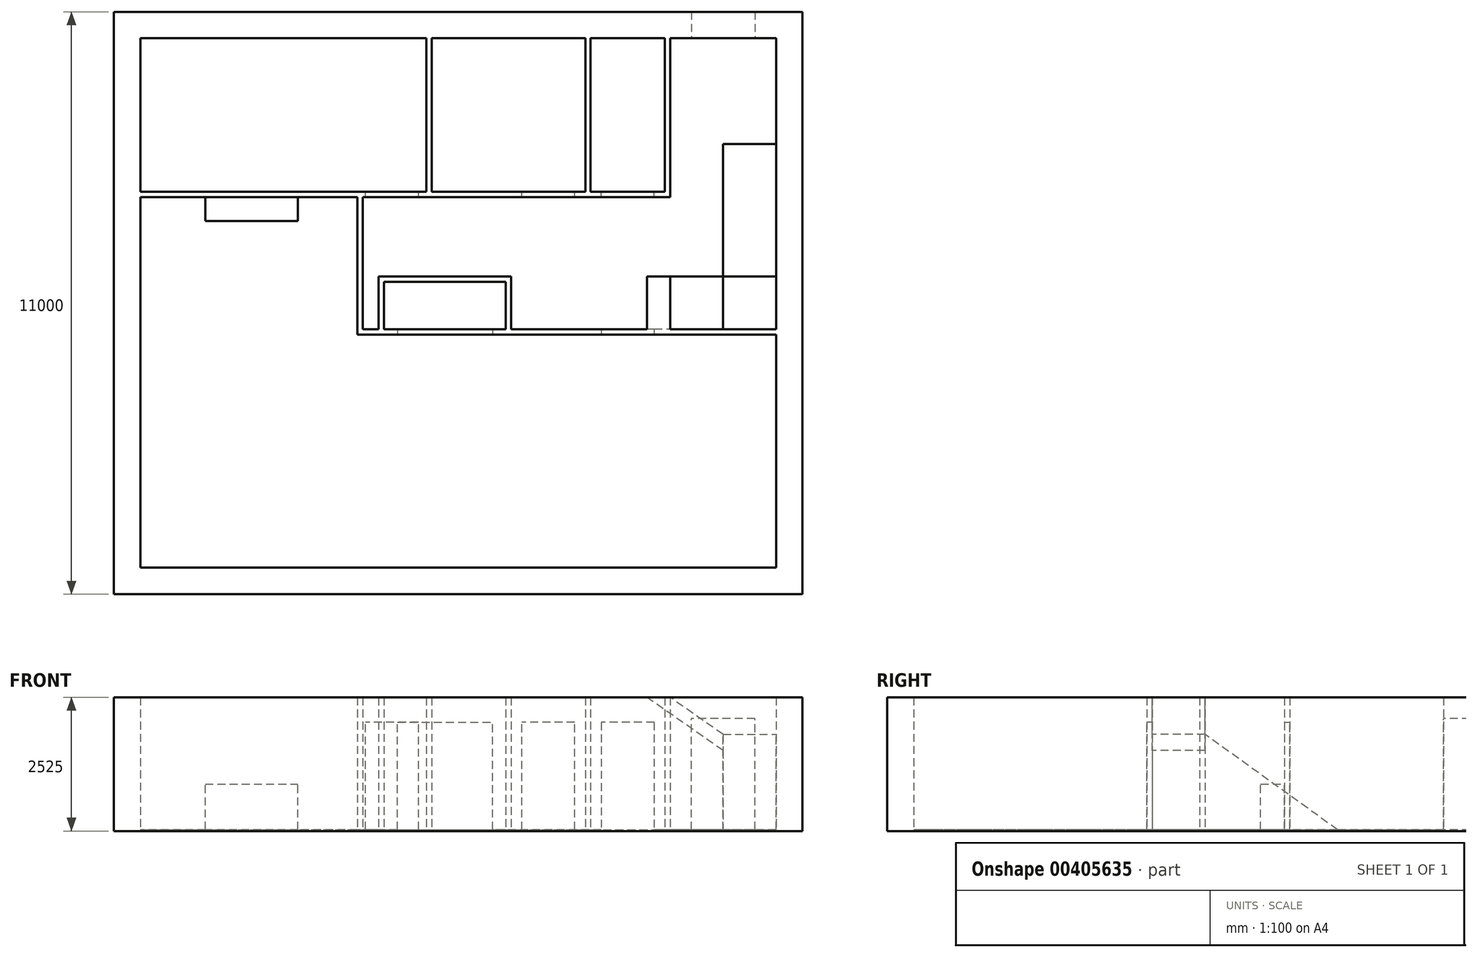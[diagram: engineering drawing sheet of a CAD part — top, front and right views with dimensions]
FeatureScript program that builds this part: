
annotation { "Feature Type Name" : "Feature", "Feature Type Description" : "" }
export const myFeature = defineFeature(function(context is Context, id is Id, definition is map)
    precondition{}
    {
        {
            var Q0;
            Q0=qCreatedBy(makeId("Top.planeOp"),FACE);
            var sketch = newSketch(context, id + "F0", { "sketchPlane" : qUnion([Q0])});
            skLineSegment(sketch, "E0.bottom", {"start": v(0, 0) * mm, "end": v(-13000, 0) * mm});
            skLineSegment(sketch, "E0.top", {"start": v(0, -11000) * mm, "end": v(-13000, -11000) * mm});
            skLineSegment(sketch, "E0.left", {"start": v(0, 0) * mm, "end": v(0, -11000) * mm});
            skLineSegment(sketch, "E0.right", {"start": v(-13000, 0) * mm, "end": v(-13000, -11000) * mm});
            skLineSegment(sketch, "E1.bottom", {"start": v(-12500, -500) * mm, "end": v(-7100, -500) * mm});
            skLineSegment(sketch, "E1.top", {"start": v(-12500, -10500) * mm, "end": v(-500, -10500) * mm});
            skLineSegment(sketch, "E1.left", {"start": v(-12500, -500) * mm, "end": v(-12500, -3400) * mm});
            skLineSegment(sketch, "E1.right", {"start": v(-500, -500) * mm, "end": v(-500, -6000) * mm});
            skLineSegment(sketch, "E2", {"start": v(-500, -6000) * mm, "end": v(-5500, -6000) * mm});
            skLineSegment(sketch, "E3", {"start": v(-8300, -6000) * mm, "end": v(-8300, -3500) * mm});
            skLineSegment(sketch, "E4", {"start": v(-8300, -3500) * mm, "end": v(-12500, -3500) * mm});
            skLineSegment(sketch, "E5", {"start": v(-8300, -3500) * mm, "end": v(-2500, -3500) * mm});
            skLineSegment(sketch, "E6", {"start": v(-2500, -3500) * mm, "end": v(-2500, -500) * mm});
            skLineSegment(sketch, "E7", {"start": v(-7000, -3400) * mm, "end": v(-7000, -500) * mm});
            skLineSegment(sketch, "E8", {"start": v(-8000, -5000) * mm, "end": v(-5500, -5000) * mm});
            skLineSegment(sketch, "E9", {"start": v(-5500, -5000) * mm, "end": v(-5500, -6000) * mm});
            skLineSegment(sketch, "E10", {"start": v(-8000, -5000) * mm, "end": v(-8000, -6000) * mm});
            skLineSegment(sketch, "E11", {"start": v(-500, -6100) * mm, "end": v(-8400, -6100) * mm});
            skLineSegment(sketch, "E12", {"start": v(-8400, -6100) * mm, "end": v(-8400, -3500) * mm});
            skLineSegment(sketch, "E13", {"start": v(-7900, -6000) * mm, "end": v(-7900, -5100) * mm});
            skLineSegment(sketch, "E14", {"start": v(-7900, -5100) * mm, "end": v(-5600, -5100) * mm});
            skLineSegment(sketch, "E15", {"start": v(-5600, -5100) * mm, "end": v(-5600, -6000) * mm});
            skLineSegment(sketch, "E16.trimOffspring", {"start": v(-8000, -6000) * mm, "end": v(-8300, -6000) * mm});
            skLineSegment(sketch, "E17.trimOffspring", {"start": v(-5600, -6000) * mm, "end": v(-7900, -6000) * mm});
            skLineSegment(sketch, "E18.trimOffspring", {"start": v(-500, -6100) * mm, "end": v(-500, -10500) * mm});
            skLineSegment(sketch, "E19", {"start": v(-12500, -3400) * mm, "end": v(-7100, -3400) * mm});
            skLineSegment(sketch, "E20", {"start": v(-2600, -3400) * mm, "end": v(-2600, -500) * mm});
            skLineSegment(sketch, "E21", {"start": v(-4100, -3400) * mm, "end": v(-4100, -500) * mm});
            skLineSegment(sketch, "E22", {"start": v(-7100, -3400) * mm, "end": v(-7100, -500) * mm});
            skLineSegment(sketch, "E23.trimOffspring", {"start": v(-7000, -500) * mm, "end": v(-4100, -500) * mm});
            skLineSegment(sketch, "E24.trimOffspring", {"start": v(-7000, -3400) * mm, "end": v(-4100, -3400) * mm});
            skLineSegment(sketch, "E25.trimOffspring", {"start": v(-4000, -3400) * mm, "end": v(-2600, -3400) * mm});
            skLineSegment(sketch, "E26", {"start": v(-4000, -3400) * mm, "end": v(-4000, -500) * mm});
            skLineSegment(sketch, "E27.trimOffspring", {"start": v(-4000, -500) * mm, "end": v(-2600, -500) * mm});
            skLineSegment(sketch, "E28.trimOffspring", {"start": v(-2500, -500) * mm, "end": v(-500, -500) * mm});
            skLineSegment(sketch, "E29.trimOffspring", {"start": v(-12500, -3500) * mm, "end": v(-12500, -10500) * mm});
            skSolve(sketch);
        }
        {
            var Q0;
            Q0 = qSketchRegion(id + "F0", true);
            extrude(context, id + "F1", {"entities" : qUnion([Q0]), "depth" : 2500 * mm});
        }
        {
            var Q0;
            Q0=makeQuery(id+"F1.opExtrude","SWEPT_FACE",FACE,{"disambiguationData":[OSD([sQuery(id+"F0.wireOp",EDGE,"E28.trimOffspring")])]});
            var sketch = newSketch(context, id + "F2", { "sketchPlane" : qUnion([Q0])});
            skLineSegment(sketch, "E30.bottom", {"start": v(-900, 0) * mm, "end": v(-2100, 0) * mm});
            skLineSegment(sketch, "E30.top", {"start": v(-900, 2100) * mm, "end": v(-2100, 2100) * mm});
            skLineSegment(sketch, "E30.left", {"start": v(-900, 0) * mm, "end": v(-900, 2100) * mm});
            skLineSegment(sketch, "E30.right", {"start": v(-2100, 0) * mm, "end": v(-2100, 2100) * mm});
            skSolve(sketch);
        }
        {
            var Q0;
            Q0 = qSketchRegion(id + "F2", true);
            extrude(context, id + "F3", {"entities" : qUnion([Q0]), "operationType" : NewBodyOperationType.REMOVE, "endBound" : BoundingType.UP_TO_NEXT, "oppositeDirection" : true, "depth" : 25 * mm});
        }
        {
            var Q0;
            Q0=makeQuery(id+"F1.opExtrude","SWEPT_FACE",FACE,{"disambiguationData":[OSD([sQuery(id+"F0.wireOp",EDGE,"E25.trimOffspring")])]});
            var sketch = newSketch(context, id + "F4", { "sketchPlane" : qUnion([Q0])});
            skLineSegment(sketch, "E31.bottom", {"start": v(2800, 0) * mm, "end": v(3800, 0) * mm});
            skLineSegment(sketch, "E31.top", {"start": v(2800, 2030) * mm, "end": v(3800, 2030) * mm});
            skLineSegment(sketch, "E31.left", {"start": v(2800, 0) * mm, "end": v(2800, 2030) * mm});
            skLineSegment(sketch, "E31.right", {"start": v(3800, 0) * mm, "end": v(3800, 2030) * mm});
            skLineSegment(sketch, "E32.bottom", {"start": v(4300, 0) * mm, "end": v(5300, 0) * mm});
            skLineSegment(sketch, "E32.top", {"start": v(4300, 2030) * mm, "end": v(5300, 2030) * mm});
            skLineSegment(sketch, "E32.left", {"start": v(4300, 0) * mm, "end": v(4300, 2030) * mm});
            skLineSegment(sketch, "E32.right", {"start": v(5300, 0) * mm, "end": v(5300, 2030) * mm});
            skLineSegment(sketch, "E33.bottom", {"start": v(7250, 0) * mm, "end": v(8250, 0) * mm});
            skLineSegment(sketch, "E33.top", {"start": v(7250, 2030) * mm, "end": v(8250, 2030) * mm});
            skLineSegment(sketch, "E33.left", {"start": v(7250, 0) * mm, "end": v(7250, 2030) * mm});
            skLineSegment(sketch, "E33.right", {"start": v(8250, 0) * mm, "end": v(8250, 2030) * mm});
            skSolve(sketch);
        }
        {
            var Q0;
            Q0 = qSketchRegion(id + "F4", true);
            extrude(context, id + "F5", {"entities" : qUnion([Q0]), "operationType" : NewBodyOperationType.REMOVE, "endBound" : BoundingType.UP_TO_NEXT, "oppositeDirection" : true, "depth" : 25 * mm});
        }
        {
            var Q0;
            Q0=makeQuery(id+"F1.opExtrude","SWEPT_FACE",FACE,{"disambiguationData":[OSD([sQuery(id+"F0.wireOp",EDGE,"E11")])]});
            var sketch = newSketch(context, id + "F6", { "sketchPlane" : qUnion([Q0])});
            skLineSegment(sketch, "E34.bottom", {"start": v(-7650, 0) * mm, "end": v(-5850, 0) * mm});
            skLineSegment(sketch, "E34.top", {"start": v(-7650, 2030) * mm, "end": v(-5850, 2030) * mm});
            skLineSegment(sketch, "E34.left", {"start": v(-7650, 0) * mm, "end": v(-7650, 2030) * mm});
            skLineSegment(sketch, "E34.right", {"start": v(-5850, 0) * mm, "end": v(-5850, 2030) * mm});
            skLineSegment(sketch, "E35.bottom", {"start": v(-3800, 0) * mm, "end": v(-2800, 0) * mm});
            skLineSegment(sketch, "E35.top", {"start": v(-3800, 2030) * mm, "end": v(-2800, 2030) * mm});
            skLineSegment(sketch, "E35.left", {"start": v(-3800, 0) * mm, "end": v(-3800, 2030) * mm});
            skLineSegment(sketch, "E35.right", {"start": v(-2800, 0) * mm, "end": v(-2800, 2030) * mm});
            skSolve(sketch);
        }
        {
            var Q0;
            Q0 = qSketchRegion(id + "F6", true);
            extrude(context, id + "F7", {"entities" : qUnion([Q0]), "operationType" : NewBodyOperationType.REMOVE, "endBound" : BoundingType.UP_TO_NEXT, "oppositeDirection" : true, "depth" : 25 * mm});
        }
        {
            var Q0;
            Q0=makeQuery(id+"F1.opExtrude","SWEPT_FACE",FACE,{"disambiguationData":[OSD([sQuery(id+"F0.wireOp",EDGE,"E4")])]});
            var sketch = newSketch(context, id + "F8", { "sketchPlane" : qUnion([Q0])});
            skLineSegment(sketch, "E36.bottom", {"start": v(-11275, 0) * mm, "end": v(-9525, 0) * mm});
            skLineSegment(sketch, "E36.top", {"start": v(-11275, 860) * mm, "end": v(-9525, 860) * mm});
            skLineSegment(sketch, "E36.left", {"start": v(-11275, 0) * mm, "end": v(-11275, 860) * mm});
            skLineSegment(sketch, "E36.right", {"start": v(-9525, 0) * mm, "end": v(-9525, 860) * mm});
            skSolve(sketch);
        }
        {
            var Q0;
            Q0 = qSketchRegion(id + "F8", true);
            extrude(context, id + "F9", {"entities" : qUnion([Q0]), "operationType" : NewBodyOperationType.ADD, "depth" : 450 * mm});
        }
        {
            var Q0;
            Q0=makeQuery(id+"F9.boolean.opBoolean","MERGE",FACE,{"derivedFrom":[makeQuery(id+"F1.opExtrude","CAP_FACE",FACE,{"disambiguationData":[OSD([sQuery(id+"F0.wireOp",EDGE,"E0.bottom"),sQuery(id+"F0.wireOp",EDGE,"E0.top"),sQuery(id+"F0.wireOp",EDGE,"E0.left"),sQuery(id+"F0.wireOp",EDGE,"E0.right"),sQuery(id+"F0.wireOp",EDGE,"E1.bottom"),sQuery(id+"F0.wireOp",EDGE,"E1.top"),sQuery(id+"F0.wireOp",EDGE,"E1.left"),sQuery(id+"F0.wireOp",EDGE,"E1.right"),sQuery(id+"F0.wireOp",EDGE,"E2"),sQuery(id+"F0.wireOp",EDGE,"E3"),sQuery(id+"F0.wireOp",EDGE,"E4"),sQuery(id+"F0.wireOp",EDGE,"E5"),sQuery(id+"F0.wireOp",EDGE,"E6"),sQuery(id+"F0.wireOp",EDGE,"E7"),sQuery(id+"F0.wireOp",EDGE,"E8"),sQuery(id+"F0.wireOp",EDGE,"E9"),sQuery(id+"F0.wireOp",EDGE,"E10"),sQuery(id+"F0.wireOp",EDGE,"E11"),sQuery(id+"F0.wireOp",EDGE,"E12"),sQuery(id+"F0.wireOp",EDGE,"E13"),sQuery(id+"F0.wireOp",EDGE,"E14"),sQuery(id+"F0.wireOp",EDGE,"E15"),sQuery(id+"F0.wireOp",EDGE,"E16.trimOffspring"),sQuery(id+"F0.wireOp",EDGE,"E17.trimOffspring"),sQuery(id+"F0.wireOp",EDGE,"E18.trimOffspring"),sQuery(id+"F0.wireOp",EDGE,"E19"),sQuery(id+"F0.wireOp",EDGE,"E20"),sQuery(id+"F0.wireOp",EDGE,"E21"),sQuery(id+"F0.wireOp",EDGE,"E22"),sQuery(id+"F0.wireOp",EDGE,"E23.trimOffspring"),sQuery(id+"F0.wireOp",EDGE,"E24.trimOffspring"),sQuery(id+"F0.wireOp",EDGE,"E25.trimOffspring"),sQuery(id+"F0.wireOp",EDGE,"E26"),sQuery(id+"F0.wireOp",EDGE,"E27.trimOffspring"),sQuery(id+"F0.wireOp",EDGE,"E28.trimOffspring"),sQuery(id+"F0.wireOp",EDGE,"E29.trimOffspring")])],"isStart":true}),makeQuery(id+"F9.opExtrude","SWEPT_FACE",FACE,{"disambiguationData":[OSD([sQuery(id+"F8.wireOp",EDGE,"E36.bottom")])]})]});
            var sketch = newSketch(context, id + "F10", { "sketchPlane" : qUnion([Q0])});
            skLineSegment(sketch, "E37.bottom", {"start": v(-13000, 11000) * mm, "end": v(0, 11000) * mm});
            skLineSegment(sketch, "E37.top", {"start": v(-13000, 0) * mm, "end": v(0, 0) * mm});
            skLineSegment(sketch, "E37.left", {"start": v(-13000, 11000) * mm, "end": v(-13000, 0) * mm});
            skLineSegment(sketch, "E37.right", {"start": v(0, 11000) * mm, "end": v(0, 0) * mm});
            skSolve(sketch);
        }
        {
            var Q0;
            Q0 = qSketchRegion(id + "F10", true);
            extrude(context, id + "F11", {"entities" : qUnion([Q0]), "operationType" : NewBodyOperationType.ADD, "depth" : 25 * mm});
        }
        {
            var Q0;
            Q0=makeQuery(id+"F1.opExtrude","SWEPT_FACE",FACE,{"disambiguationData":[OSD([sQuery(id+"F0.wireOp",EDGE,"E1.right")])]});
            var sketch = newSketch(context, id + "F12", { "sketchPlane" : qUnion([Q0])});
            skLineSegment(sketch, "E38", {"start": v(6000, 0) * mm, "end": v(2500, 0) * mm});
            skLineSegment(sketch, "E39", {"start": v(2500, 0) * mm, "end": v(5000, 1800) * mm});
            skLineSegment(sketch, "E40", {"start": v(5000, 1800) * mm, "end": v(6000, 1800) * mm});
            skLineSegment(sketch, "E41", {"start": v(6000, 1800) * mm, "end": v(6000, 0) * mm});
            skSolve(sketch);
        }
        {
            var Q0;
            Q0 = qSketchRegion(id + "F12", true);
            extrude(context, id + "F13", {"entities" : qUnion([Q0]), "operationType" : NewBodyOperationType.ADD, "depth" : 1000 * mm});
        }
        {
            var Q0;
            Q0=makeQuery(id+"F1.opExtrude","SWEPT_FACE",FACE,{"disambiguationData":[OSD([sQuery(id+"F0.wireOp",EDGE,"E2")])]});
            var sketch = newSketch(context, id + "F14", { "sketchPlane" : qUnion([Q0])});
            skLineSegment(sketch, "E42", {"start": v(1500, 1800) * mm, "end": v(2500, 2500) * mm});
            skLineSegment(sketch, "E43", {"start": v(1500, 1494.84) * mm, "end": v(2935.95, 2500) * mm});
            skLineSegment(sketch, "E44", {"start": v(2500, 2500) * mm, "end": v(2935.95, 2500) * mm});
            skLineSegment(sketch, "E45", {"start": v(1500, 1800) * mm, "end": v(1500, 1494.84) * mm});
            skSolve(sketch);
        }
        {
            var Q0;
            Q0 = qSketchRegion(id + "F14", true);
            extrude(context, id + "F15", {"entities" : qUnion([Q0]), "operationType" : NewBodyOperationType.ADD, "depth" : 1000 * mm});
        }
    });
